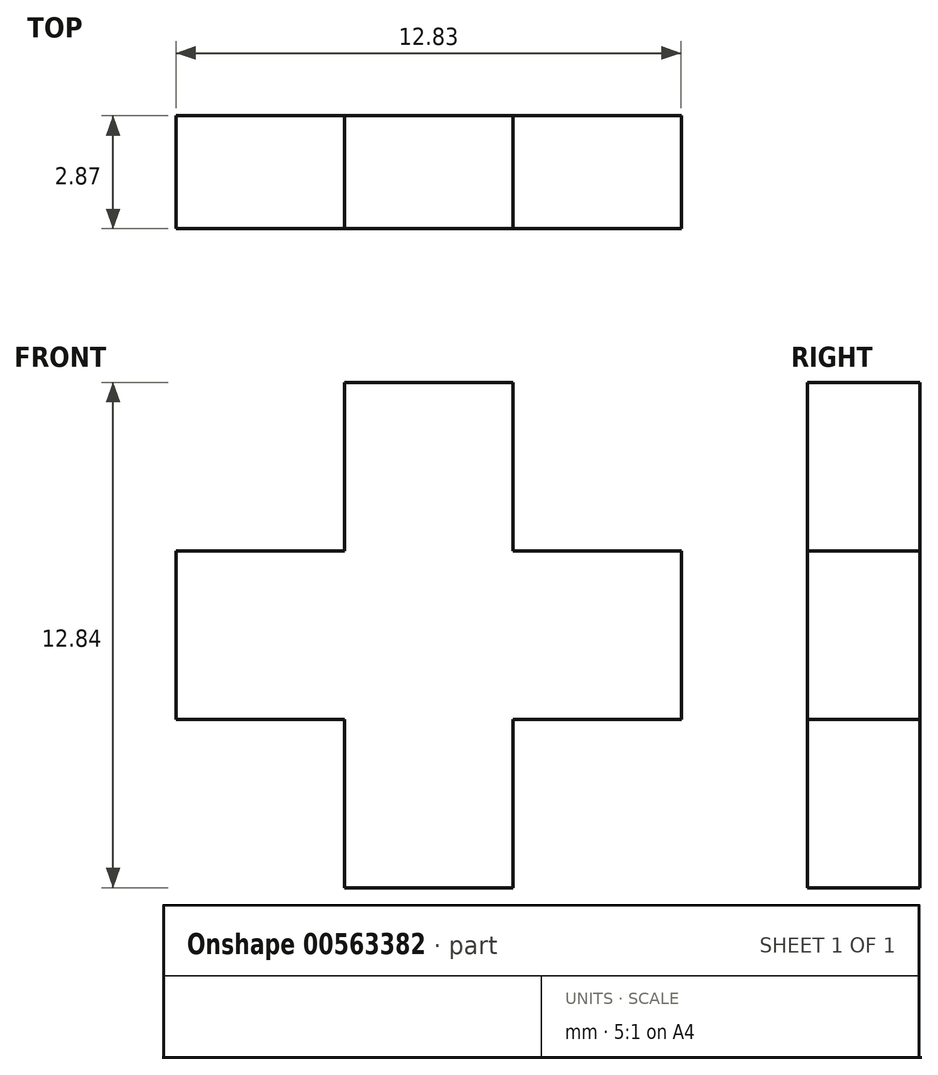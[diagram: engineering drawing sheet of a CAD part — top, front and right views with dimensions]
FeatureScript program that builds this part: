
annotation { "Feature Type Name" : "Feature", "Feature Type Description" : "" }
export const myFeature = defineFeature(function(context is Context, id is Id, definition is map)
    precondition{}
    {
        {
            var Q0;
            Q0=qCreatedBy(makeId("Front.planeOp"),FACE);
            var sketch = newSketch(context, id + "F0", { "sketchPlane" : qUnion([Q0])});
            skLineSegment(sketch, "E0", {"start": v(-37.22, 28.1) * mm, "end": v(-37.22, 23.82) * mm});
            skLineSegment(sketch, "E1", {"start": v(-37.22, 23.82) * mm, "end": v(-41.5, 23.82) * mm});
            skLineSegment(sketch, "E2", {"start": v(-41.5, 23.82) * mm, "end": v(-41.5, 19.54) * mm});
            skLineSegment(sketch, "E3", {"start": v(-41.5, 19.54) * mm, "end": v(-37.22, 19.54) * mm});
            skLineSegment(sketch, "E4", {"start": v(-37.22, 19.54) * mm, "end": v(-37.22, 15.26) * mm});
            skLineSegment(sketch, "E5", {"start": v(-37.22, 15.26) * mm, "end": v(-32.95, 15.26) * mm});
            skLineSegment(sketch, "E6", {"start": v(-32.95, 15.26) * mm, "end": v(-32.95, 19.54) * mm});
            skLineSegment(sketch, "E7", {"start": v(-32.95, 19.54) * mm, "end": v(-28.67, 19.54) * mm});
            skLineSegment(sketch, "E8", {"start": v(-28.67, 19.54) * mm, "end": v(-28.67, 23.82) * mm});
            skLineSegment(sketch, "E9", {"start": v(-28.67, 23.82) * mm, "end": v(-32.95, 23.82) * mm});
            skLineSegment(sketch, "E10", {"start": v(-32.95, 23.82) * mm, "end": v(-32.95, 28.1) * mm});
            skLineSegment(sketch, "E11", {"start": v(-32.95, 28.1) * mm, "end": v(-37.22, 28.1) * mm});
            skSolve(sketch);
        }
        {
            var Q0;
            Q0=qSketchRegion(id+"F0",true);
            extrude(context, id + "F1", {"entities" : qUnion([Q0]), "depth" : 2.87 * mm});
        }
    });
